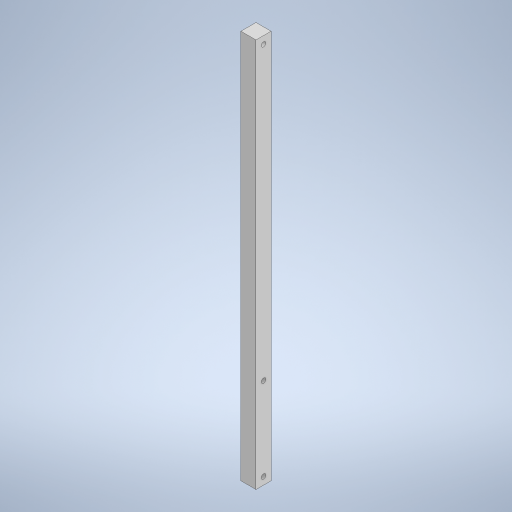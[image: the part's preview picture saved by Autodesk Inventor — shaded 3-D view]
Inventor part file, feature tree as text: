
AUTODESK INVENTOR PART (.ipt)
format: ipt  version: 2023 (Build 270158000, 158)  size: 243,712 bytes
history: native  units: mm
features: sketch x2, other x1, extrude x1, hole x1
ambient origin geometry x8: Origin, YZ Plane, XZ Plane, XY Plane, X Axis, Y Axis, Z Axis, Center Point
bodies: Body1 (feature_tree)
feature tree (5):
  other  "ソリッド1"
  extrude  "押し出し1"  Depth=258.0mm
  hole  "穴1"  [1 undecoded]
  sketch  "スケッチ1"
  sketch  "スケッチ2"
note: 1 required parameter value undecoded (feature->parameter linkage not recoverable at this tier; creation-order binding heuristic only, values carry confidence <= 0.55)
